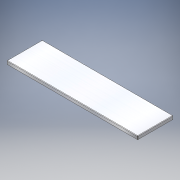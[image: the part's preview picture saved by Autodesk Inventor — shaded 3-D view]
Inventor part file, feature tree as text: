
AUTODESK INVENTOR PART (.ipt)
format: ipt  version: 2017 (Build 210142000, 142)  size: 350,208 bytes
history: native  units: mm
features: sheet_metal_op x8, sketch x7, other x5, plane x1
ambient origin geometry x8: Origin, YZ Plane, XZ Plane, XY Plane, X Axis, Y Axis, Z Axis, Center Point
bodies: Solid1 (feature_tree)
feature tree (21):
  sheet_metal_op  "Face1"
  sheet_metal_op  "Flange1"
  sheet_metal_op  "Hem1"
  sheet_metal_op  "Hem2"
  sheet_metal_op  "Hem3"
  sheet_metal_op  "Hem4"
  plane  "Work Plane1"
  other  "Decal1"
  sketch  "Sketch1"  dims[d0=253.299mm]
  other  "Plate1"
  sketch  "Sketch2"  dims[d1=933.598mm]
  other  "Plate2"
  sheet_metal_op  "Bend1"
  sheet_metal_op  "Corner1"
  sketch  "Sketch7"  dims[d6=1.5mm d7=25.0mm d8=90.0deg d9=1.5mm d10=6.0mm d11=1.5mm d12=1.5mm d13=1.5mm d14=0.75mm d15=3.0mm d16=1.5mm d17=10.0mm d18=0.75mm d19=0.375mm d20=1.5mm d21=0.75mm d22=3.0mm d23=1.5mm d24=10.0mm d25=0.75mm d26=0.375mm d27=1.5mm d28=0.75mm d29=3.0mm d30=1.5mm d31=245.0mm d32=10.0mm d33=0.75mm d34=0.375mm d35=1.5mm d36=0.75mm d37=3.0mm d38=1.5mm d39=245.0mm d40=10.0mm d41=0.75mm d42=0.375mm d43=200.0mm]
  other  "Image1"
  sketch  "Sketch3"  dims[d2=1.5mm]
  sketch  "Sketch4"  dims[d3=1.5mm]
  sketch  "Sketch5"  dims[d4=0.75mm]
  sketch  "Sketch6"  dims[d5=3.0mm]
  other  "Definition1"
